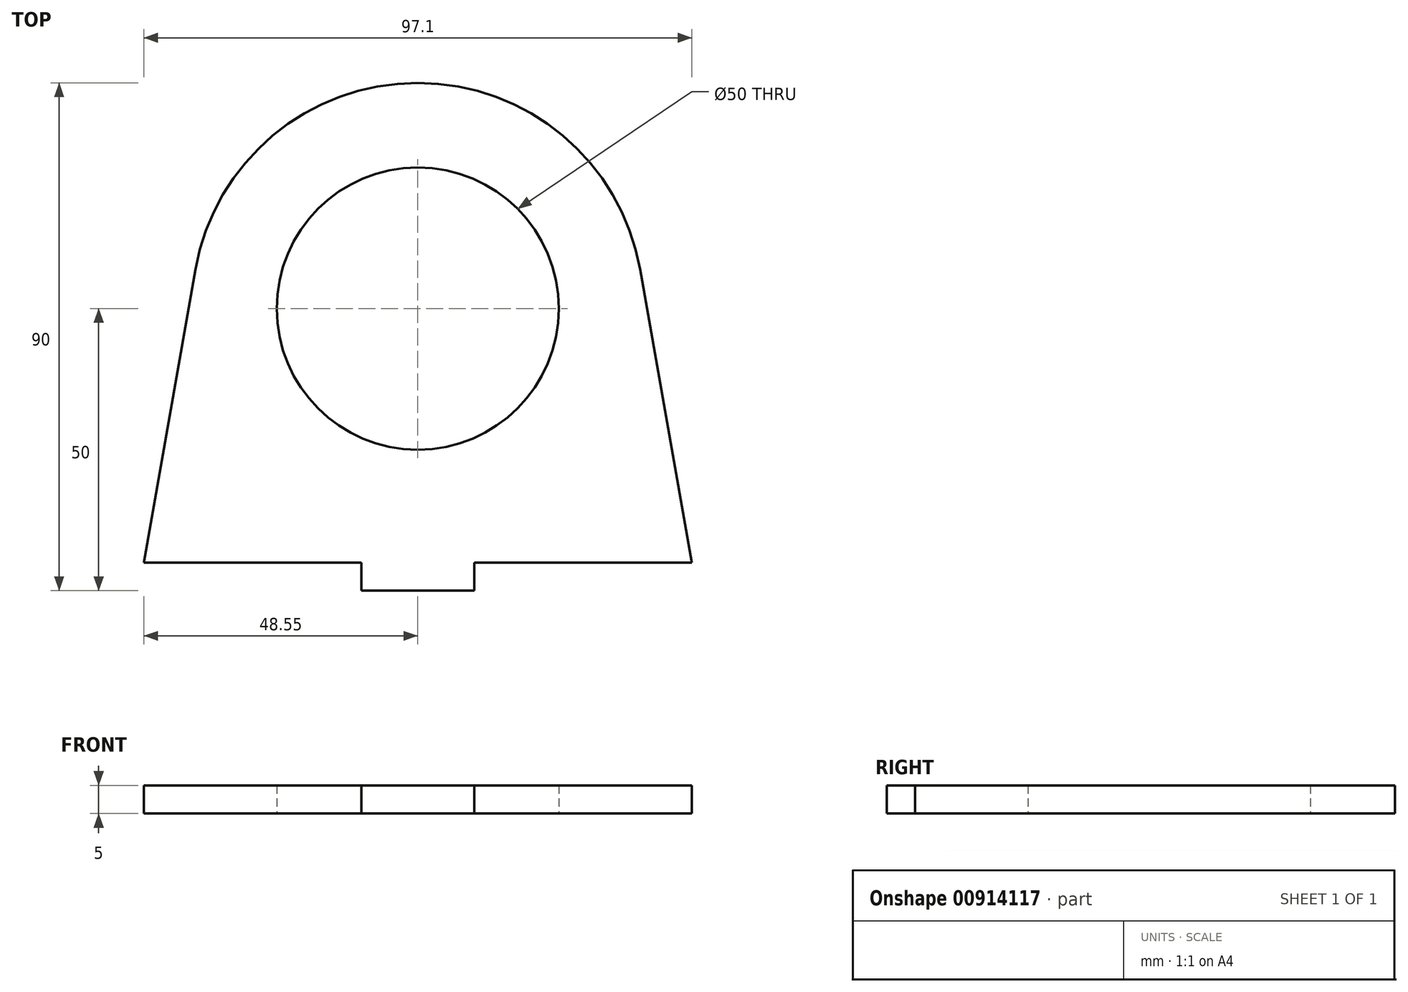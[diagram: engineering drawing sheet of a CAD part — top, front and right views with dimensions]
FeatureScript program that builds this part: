
annotation { "Feature Type Name" : "Feature", "Feature Type Description" : "" }
export const myFeature = defineFeature(function(context is Context, id is Id, definition is map)
    precondition{}
    {
        {
            var Q0;
            Q0=qCreatedBy(makeId("Top.planeOp"),FACE);
            var sketch = newSketch(context, id + "F0", { "sketchPlane" : qUnion([Q0])});
            skLineSegment(sketch, "E0", {"start": v(-48.55, 0) * mm, "end": v(-39.4, 51.95) * mm});
            skArc(sketch, "E1", {"start": v(39.4, 51.95) * mm, "mid": v(0, 85) * mm, "end": v(-39.4, 51.95) * mm});
            skLineSegment(sketch, "E2", {"start": v(39.4, 51.95) * mm, "end": v(48.55, 0) * mm});
            skLineSegment(sketch, "E3", {"start": v(-48.55, 0) * mm, "end": v(-10.2, 0) * mm});
            skLineSegment(sketch, "E4", {"start": v(-10, -0.2) * mm, "end": v(-10, -5) * mm});
            skLineSegment(sketch, "E5", {"start": v(-10, -5) * mm, "end": v(10, -5) * mm});
            skLineSegment(sketch, "E6", {"start": v(10, -5) * mm, "end": v(10, -0.2) * mm});
            skLineSegment(sketch, "E7.trimOffspring", {"start": v(10.2, 0) * mm, "end": v(48.55, 0) * mm});
            skPoint(sketch, "E8.visualSharp", {"position": v(-10, 0) * mm});
            skArc(sketch, "E8.filletArc", {"start": v(-10, -0.2) * mm, "mid": v(-10.06, -0.06) * mm, "end": v(-10.2, 0) * mm});
            skPoint(sketch, "E9.visualSharp", {"position": v(10, 0) * mm});
            skArc(sketch, "E9.filletArc", {"start": v(10.2, 0) * mm, "mid": v(10.06, -0.06) * mm, "end": v(10, -0.2) * mm});
            skCircle(sketch, "E10", {"center": v(0, 45) * mm, "radius": 25 * mm});
            skSolve(sketch);
        }
        {
            var Q0;
            Q0 = qSketchRegion(id + "F0", true);
            extrude(context, id + "F1", {"entities" : qUnion([Q0]), "depth" : 5 * mm, "offsetDistance" : 25 * mm});
        }
    });
